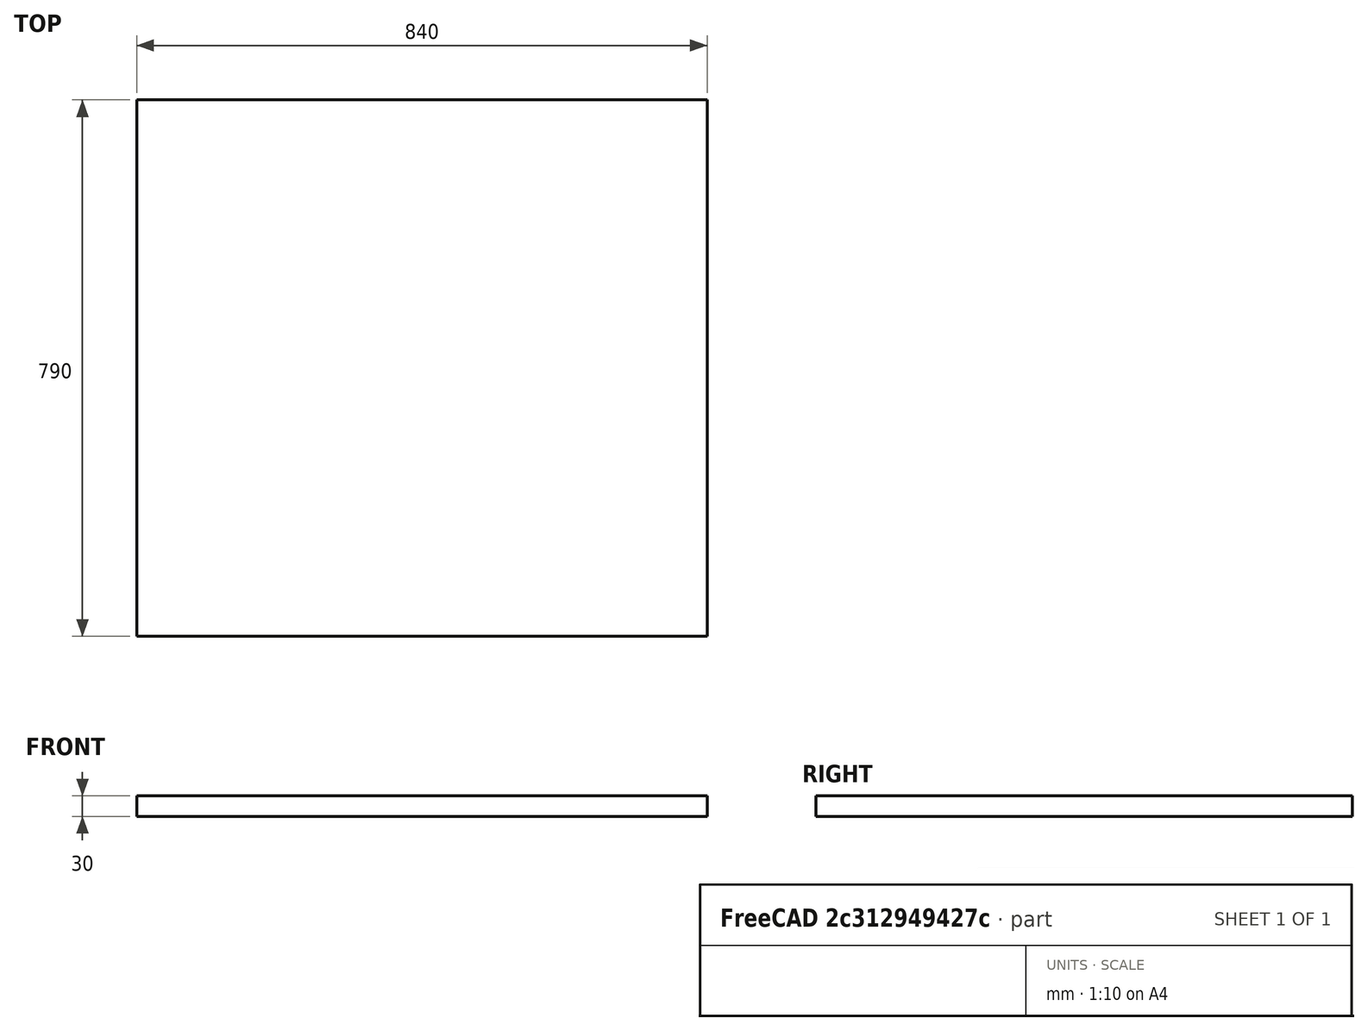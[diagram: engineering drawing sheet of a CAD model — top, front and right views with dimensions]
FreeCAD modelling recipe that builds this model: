
FCSTD DOCUMENT  (FreeCAD 0.20R29603 (Git))
Label: UnerbodenVorne
License: All rights reserved
LicenseURL: http://en.wikipedia.org/wiki/All_rights_reserved
objects: Sketcher::SketchObject×1, PartDesign::Pad×1, PartDesign::Body×1
note: 4 computed .brp shape members not serialized (recipe doc carries the construction recipe); baked Part::Feature solids carry a one-line shape summary decoded from their .brp

FEATURE [Sketcher::SketchObject] Sketch
  FullyConstrained = true
  MapMode = 5
  Support = -> [XY_Plane]
  sketch-geometry (5):
    g0: LineSegment StartX=-420 StartY=395 StartZ=0 EndX=-420 EndY=-395 EndZ=0
    g1: LineSegment StartX=-420 StartY=-395 StartZ=0 EndX=420 EndY=-395 EndZ=0
    g2: LineSegment StartX=420 StartY=-395 StartZ=0 EndX=420 EndY=395 EndZ=0
    g3: LineSegment StartX=420 StartY=395 StartZ=0 EndX=-420 EndY=395 EndZ=0
    g4: GeomPoint X=0 Y=0 Z=0
  constraints (12):
    c: Coincident(g0,g1)
    c: Coincident(g1,g2)
    c: Coincident(g2,g3)
    c: Coincident(g3,g0)
    c: Horizontal(g1)
    c: Horizontal(g3)
    c: Vertical(g0)
    c: Vertical(g2)
    c: Symmetric(g1,g0,g4)
    c: Coincident(g4,g-1)
    c: Distance(g3) = 840
    c: Distance(g2) = 790
FEATURE [PartDesign::Pad] Pad
  Direction = (0,0,1)
  Length = 30
  Length2 = 10
  Profile = -> Sketch
  ReferenceAxis = -> Sketch [N_Axis]
  Type = 0
FEATURE [PartDesign::Body] Body
  Group = -> [Sketch,Pad]
  Origin = -> Origin
  Tip = -> Pad
